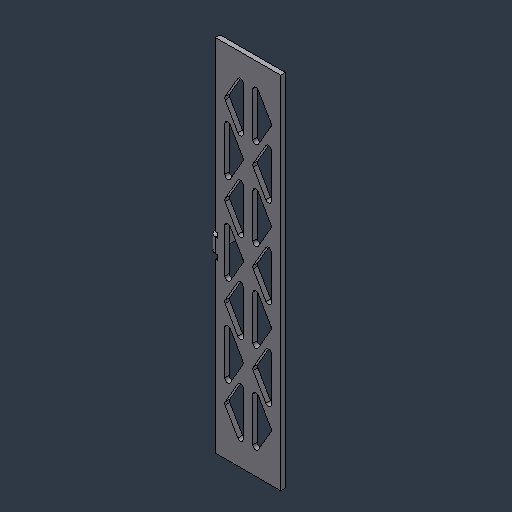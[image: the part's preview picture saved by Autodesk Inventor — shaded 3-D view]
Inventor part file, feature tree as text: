
AUTODESK INVENTOR PART (.ipt)
format: ipt  version: 2024.3 (Build 283343000, 343)  size: 288,768 bytes
history: native  units: mm (DEFAULTED — no unit token found)
features: sheet_metal_op x4, sketch x3, other x3, mirror x1
ambient origin geometry x8: Origin, YZ Plane, XZ Plane, XY Plane, X Axis, Y Axis, Z Axis, Center Point
bodies: Solid1 (feature_tree)
feature tree (11):
  sheet_metal_op  "Face1"
  mirror  "Mirror1"
  sheet_metal_op  "Flange1"
  sketch  "Sketch2"  dims[d0=44.45mm]
  other  "Plate1"
  sketch  "Sketch3"  dims[d1=245.0mm]
  sketch  "Sketch4"  dims[d2=3.175mm d3=2.0mm d4=6.35mm d5=30.0deg d6=30.0mm d7=2.0mm d8=30.0deg d10=15.0mm d11=20.0mm d13=60.0mm d14=10.0mm d16=10.0mm d18=60.0mm d19=3.175mm d20=0.0mm d21=3.175mm d22=1.5875mm d23=6.35mm d24=4.7625mm d25=10.0mm d26=15.0mm d27=90.0deg d28=1.0mm d29=12.7mm d30=3.175mm d31=4.7625mm]
  other  "Plate2"
  sheet_metal_op  "Bend1"
  sheet_metal_op  "Corner1"
  other  "Cut1"
